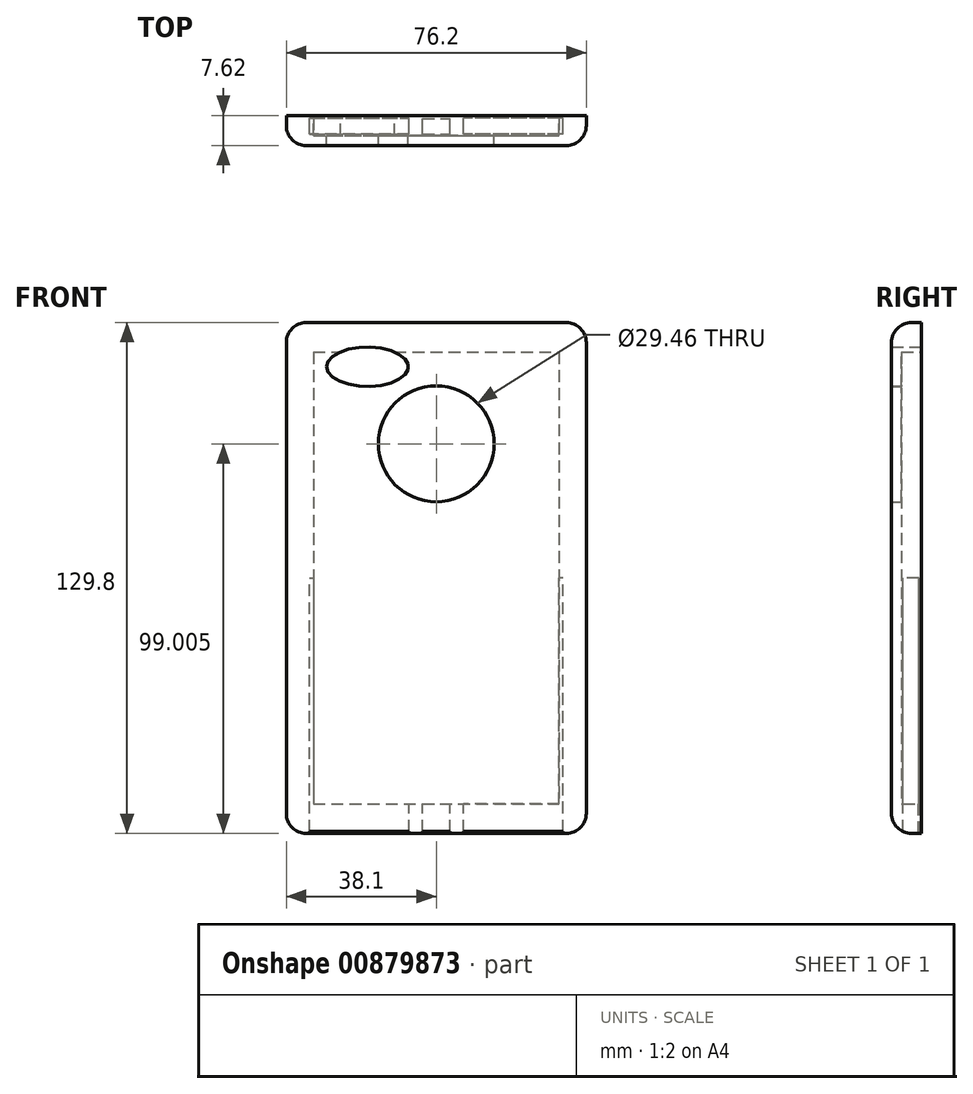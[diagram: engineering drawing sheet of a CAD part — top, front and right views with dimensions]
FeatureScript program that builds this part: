
annotation { "Feature Type Name" : "Feature", "Feature Type Description" : "" }
export const myFeature = defineFeature(function(context is Context, id is Id, definition is map)
    precondition{}
    {
        {
            var Q0;
            Q0=qCreatedBy(makeId("Front.planeOp"),FACE);
            var sketch = newSketch(context, id + "F0", { "sketchPlane" : qUnion([Q0])});
            skLineSegment(sketch, "E0.bottom", {"start": v(-38.1, 64.9) * mm, "end": v(38.1, 64.9) * mm});
            skLineSegment(sketch, "E0.top", {"start": v(-38.1, -64.9) * mm, "end": v(38.1, -64.9) * mm});
            skLineSegment(sketch, "E0.left", {"start": v(-38.1, 64.9) * mm, "end": v(-38.1, -64.9) * mm});
            skLineSegment(sketch, "E0.right", {"start": v(38.1, 64.9) * mm, "end": v(38.1, -64.9) * mm});
            skPoint(sketch, "E0.middle", {"position": v(0, 0) * mm});
            skSolve(sketch);
        }
        {
            var Q0;
            Q0 = qSketchRegion(id + "F0", true);
            extrude(context, id + "F1", {"entities" : qUnion([Q0]), "depth" : 7.62 * mm, "offsetDistance" : 25.4 * mm});
        }
        {
            var Q0;
            Q0=qCreatedBy(makeId("Front.planeOp"),FACE);
            var sketch = newSketch(context, id + "F2", { "sketchPlane" : qUnion([Q0])});
            skLineSegment(sketch, "E1.bottom", {"start": v(-31.23, 57.42) * mm, "end": v(31.23, 57.42) * mm});
            skLineSegment(sketch, "E1.top", {"start": v(-31.23, -57.42) * mm, "end": v(31.23, -57.42) * mm});
            skLineSegment(sketch, "E1.left", {"start": v(-31.23, 57.42) * mm, "end": v(-31.23, -57.42) * mm});
            skLineSegment(sketch, "E1.right", {"start": v(31.23, 57.42) * mm, "end": v(31.23, -57.42) * mm});
            skPoint(sketch, "E1.middle", {"position": v(0, 0) * mm});
            skSolve(sketch);
        }
        {
            var Q0;
            Q0 = qSketchRegion(id + "F2", true);
            extrude(context, id + "F3", {"entities" : qUnion([Q0]), "operationType" : NewBodyOperationType.REMOVE, "depth" : 5.08 * mm, "offsetDistance" : 25.4 * mm});
        }
        {
            var Q0;
            Q0=makeQuery(id+"F1.opExtrude","CAP_EDGE",EDGE,{"disambiguationData":[OSD([sQuery(id+"F0.wireOp",EDGE,"E0.right")])],"isStart":false});
            var Q1;
            Q1=makeQuery(id+"F1.opExtrude","CAP_EDGE",EDGE,{"disambiguationData":[OSD([sQuery(id+"F0.wireOp",EDGE,"E0.bottom")])],"isStart":false});
            var Q2;
            Q2=makeQuery(id+"F1.opExtrude","CAP_EDGE",EDGE,{"disambiguationData":[OSD([sQuery(id+"F0.wireOp",EDGE,"E0.left")])],"isStart":false});
            var Q3;
            Q3=makeQuery(id+"F1.opExtrude","CAP_EDGE",EDGE,{"disambiguationData":[OSD([sQuery(id+"F0.wireOp",EDGE,"E0.top")])],"isStart":false});
            var Q4;
            Q4=makeQuery(id+"F1.opExtrude","SWEPT_EDGE",EDGE,{"disambiguationData":[OSD([sQuery(id+"F0.wireOp",EDGE,"E0.top"),sQuery(id+"F0.wireOp",EDGE,"E0.left")])]});
            var Q5;
            Q5=makeQuery(id+"F1.opExtrude","SWEPT_EDGE",EDGE,{"disambiguationData":[OSD([sQuery(id+"F0.wireOp",EDGE,"E0.top"),sQuery(id+"F0.wireOp",EDGE,"E0.right")])]});
            var Q6;
            Q6=makeQuery(id+"F1.opExtrude","SWEPT_EDGE",EDGE,{"disambiguationData":[OSD([sQuery(id+"F0.wireOp",EDGE,"E0.bottom"),sQuery(id+"F0.wireOp",EDGE,"E0.left")])]});
            var Q7;
            Q7=makeQuery(id+"F1.opExtrude","SWEPT_EDGE",EDGE,{"disambiguationData":[OSD([sQuery(id+"F0.wireOp",EDGE,"E0.bottom"),sQuery(id+"F0.wireOp",EDGE,"E0.right")])]});
            fillet(context, id + "F4", {"entities" : qUnion([Q0, Q1, Q2, Q3, Q4, Q5, Q6, Q7]), "radius" : 5.08 * mm, "tangentPropagation" : true, "allowEdgeOverflow" : false});
        }
        {
            var Q0;
            Q0=qCreatedBy(makeId("Front.planeOp"),FACE);
            var sketch = newSketch(context, id + "F5", { "sketchPlane" : qUnion([Q0])});
            skCircle(sketch, "E2", {"center": v(0, 34.1) * mm, "radius": 14.73 * mm});
            skSolve(sketch);
        }
        {
            var Q0;
            Q0 = qSketchRegion(id + "F5", true);
            extrude(context, id + "F6", {"entities" : qUnion([Q0]), "operationType" : NewBodyOperationType.REMOVE, "endBound" : BoundingType.THROUGH_ALL, "depth" : 25.4 * mm, "offsetDistance" : 25.4 * mm});
        }
        {
            var Q0;
            Q0=qCreatedBy(makeId("Top.planeOp"),FACE);
            var sketch = newSketch(context, id + "F7", { "sketchPlane" : qUnion([Q0])});
            skLineSegment(sketch, "E3.bottom", {"start": v(-32.23, -4.74) * mm, "end": v(-6.9, -4.74) * mm});
            skLineSegment(sketch, "E3.top", {"start": v(-32.23, -0.7) * mm, "end": v(-6.9, -0.7) * mm});
            skLineSegment(sketch, "E3.left", {"start": v(-32.23, -4.74) * mm, "end": v(-32.23, -0.7) * mm});
            skLineSegment(sketch, "E3.right", {"start": v(-6.9, -4.74) * mm, "end": v(-6.9, -0.7) * mm});
            skPoint(sketch, "E3.middle", {"position": v(-19.56, -2.72) * mm});
            skLineSegment(sketch, "E4.MirrorCS", {"start": v(6.9, -4.74) * mm, "end": v(6.9, -0.7) * mm});
            skLineSegment(sketch, "E5.MirrorCS", {"start": v(32.23, -4.74) * mm, "end": v(6.9, -4.74) * mm});
            skLineSegment(sketch, "E6.MirrorCS", {"start": v(32.23, -0.7) * mm, "end": v(6.9, -0.7) * mm});
            skLineSegment(sketch, "E7.MirrorCS", {"start": v(32.23, -4.74) * mm, "end": v(32.23, -0.7) * mm});
            skLineSegment(sketch, "E8.bottom", {"start": v(-3.5, -4.67) * mm, "end": v(3.5, -4.67) * mm});
            skLineSegment(sketch, "E8.top", {"start": v(-3.5, -0.8) * mm, "end": v(3.5, -0.8) * mm});
            skLineSegment(sketch, "E8.left", {"start": v(-3.5, -4.67) * mm, "end": v(-3.5, -0.8) * mm});
            skLineSegment(sketch, "E8.right", {"start": v(3.5, -4.67) * mm, "end": v(3.5, -0.8) * mm});
            skPoint(sketch, "E8.middle", {"position": v(0, -2.74) * mm});
            skSolve(sketch);
        }
        {
            var Q0;
            Q0 = qSketchRegion(id + "F7", true);
            extrude(context, id + "F8", {"entities" : qUnion([Q0]), "operationType" : NewBodyOperationType.REMOVE, "endBound" : BoundingType.THROUGH_ALL, "oppositeDirection" : true, "depth" : 25.4 * mm, "offsetDistance" : 25.4 * mm});
        }
        {
            var Q0;
            Q0=qCreatedBy(makeId("Front.planeOp"),FACE);
            var sketch = newSketch(context, id + "F9", { "sketchPlane" : qUnion([Q0])});
            skEllipse(sketch, "E9", {"center": v(-17.5, 53.68) * mm, "majorRadius": 10.36 * mm, "minorRadius": 5 * mm, "majorAxis": v(-1, 0)});
            skSolve(sketch);
        }
        {
            var Q0;
            Q0 = qSketchRegion(id + "F9", true);
            extrude(context, id + "F10", {"entities" : qUnion([Q0]), "operationType" : NewBodyOperationType.REMOVE, "endBound" : BoundingType.THROUGH_ALL, "depth" : 25.4 * mm, "offsetDistance" : 25.4 * mm});
        }
    });
